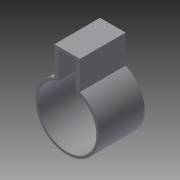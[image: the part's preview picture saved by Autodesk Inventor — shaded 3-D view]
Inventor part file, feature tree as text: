
AUTODESK INVENTOR PART (.ipt)
format: ipt  version: 2015 (Build 190159000, 159)  size: 162,304 bytes
history: native  units: in
note: dims shown in document units (in); Inventor stores cm internally (conversion verified against a paired STEP export)
features: reference x4, extrude x3, sketch x3, plane x1
ambient origin geometry x8: Origin, YZ Plane, XZ Plane, XY Plane, X Axis, Y Axis, Z Axis, Center Point
bodies: Solid1 (feature_tree)
feature tree (11):
  plane  "Work Plane1"
  extrude  "Extrusion1"  Depth=0.1969in
  extrude  "Extrusion2"  Depth=0.1181in
  extrude  "Extrusion3"  Depth=1.9685in TaperAngle=0.0deg
  sketch  "Sketch1"  dims[d0=0.409in d2=0.1969in d3=0.1969in d5=0.3937in]
  reference  "Reference6"
  reference  "Reference7"
  reference  "Reference8"
  reference  "Reference9"
  sketch  "Sketch2"  dims[d6=0.1969in d7=0.0in d8=0.1181in]
  sketch  "Sketch3"  dims[d9=0.1181in d10=1.9685in d11=0.0in d12=0.1969in d13=0.0in]
